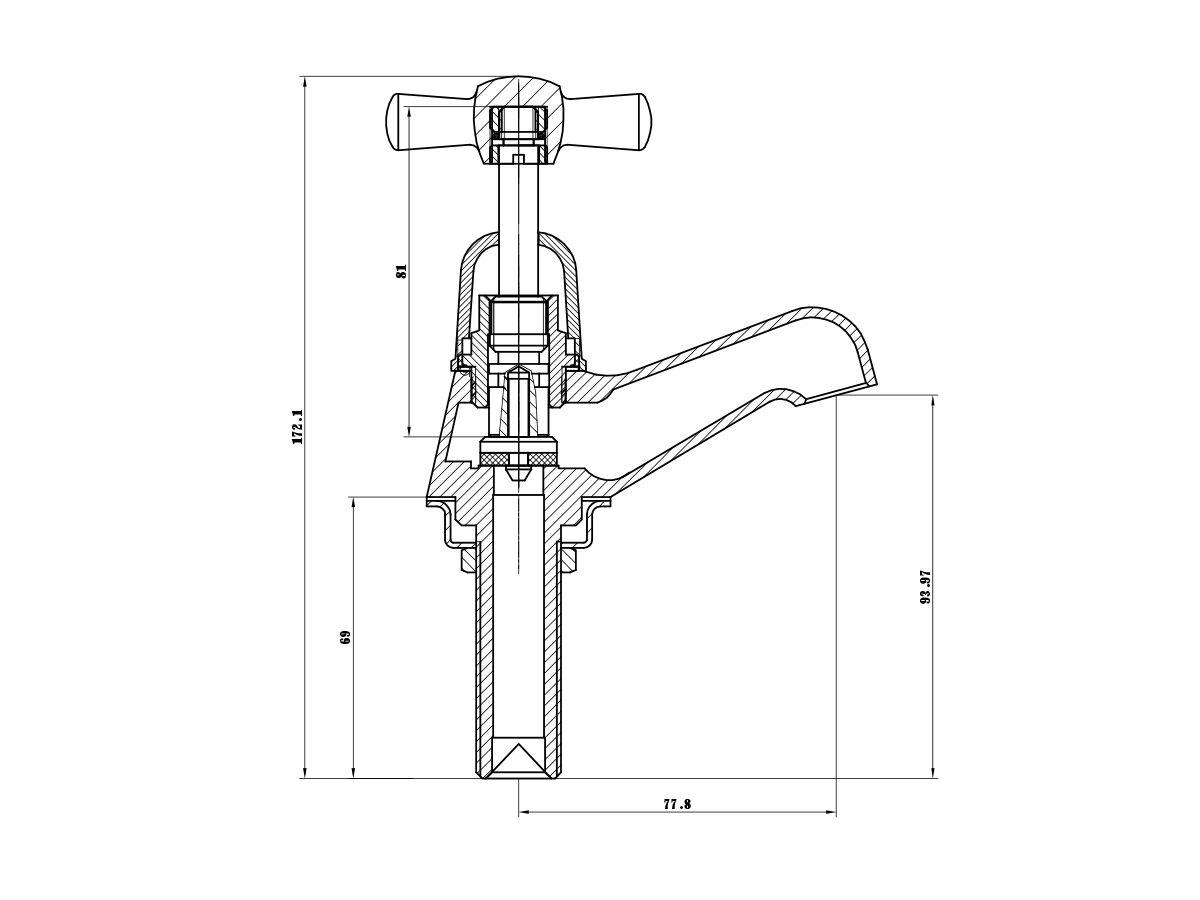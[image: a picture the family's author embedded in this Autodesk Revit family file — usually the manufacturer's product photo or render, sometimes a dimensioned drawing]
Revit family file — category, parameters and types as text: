
# Revit family: Reece_Tap_Base_Pillar Tap_Anti-Vandal
name_source: partatom
category: Plumbing Fixtures
revit_build: Autodesk Revit 2018 (Build: 20190510_1515(x64)
units: mm (PartAtom-declared; Revit-internal decimal feet)

## family parameters
Cut with Voids When Loaded = No
Host = Face
Part Type = Normal
Room Calculation Point = Yes
Round Connector Dimension = Use Diameter
Shared = Yes

## types (1)
- 77.8 mm_Chrome
    CWFU = 0
    Default Elevation = 1000 mm  [stored 3.28084 ft]
    Description = Base Pillar Taps (AV) Chrome (3 Star)
    Disclaimer = THIS FILE IS THE PROPERTY OF THE REECE GROUP. IT MAY NOT BE REPRODUCED, REVERSE-ENGINEERED OR MODIFIED. ANY REPUBLICATION, TRANSMISSION OR DISTRIBUTION FOR THE PURPOSE OF COMMERCIALLY EXPLOITING THE FILES IS PROHIBITED.
    HWFU = 0
    Keynote = Product #2216699, Reece_Tap_Base_Pillar Tap_Anti-Vandal - 77.8 mm_Chrome
    Manufacturer = Base
    Model = Base
    Reece_Detail_Additional = Pillar Tap
    Reece_Detail_Disclaimer = THIS FILE IS THE PROPERTY OF THE REECE GROUP. IT MAY NOT BE REPRODUCED, REVERSE-ENGINEERED OR MODIFIED. ANY REPUBLICATION, TRANSMISSION OR DISTRIBUTION FOR THE PURPOSE OF COMMERCIALLY EXPLOITING THE FILES IS PROHIBITED.
    Reece_Detail_Function = Anti-Vandal
    Reece_Material-Main = Reece_Brass_Chrome
    Reece_Product_Brand = Base
    Reece_Product_Description = Base Pillar Taps (AV) Chrome (3 Star)
    Reece_Product_Mount = Hob Mounted
    Reece_Product_Number = 2216699
    Reece_Product_Sub Brand = Base
    Reece_Product_Type = Tap
    Reece_Product_Web Page = https://www.reece.com.au
    Reece_Tap_Clearance = 78 mm
    Reece_Tap_Inlet = 12 mm  [stored 0.0393701 ft]
    Type Comments = Tap
    URL = https://www.reece.com.au
    WFU = 0

note: [stored X ft] marks values corroborated as IEEE doubles in the binary element streams (Revit-internal decimal feet)

## geometry (parser evidence)
native form markers: Sweep x3
no freeform markers — native parametric forms only
